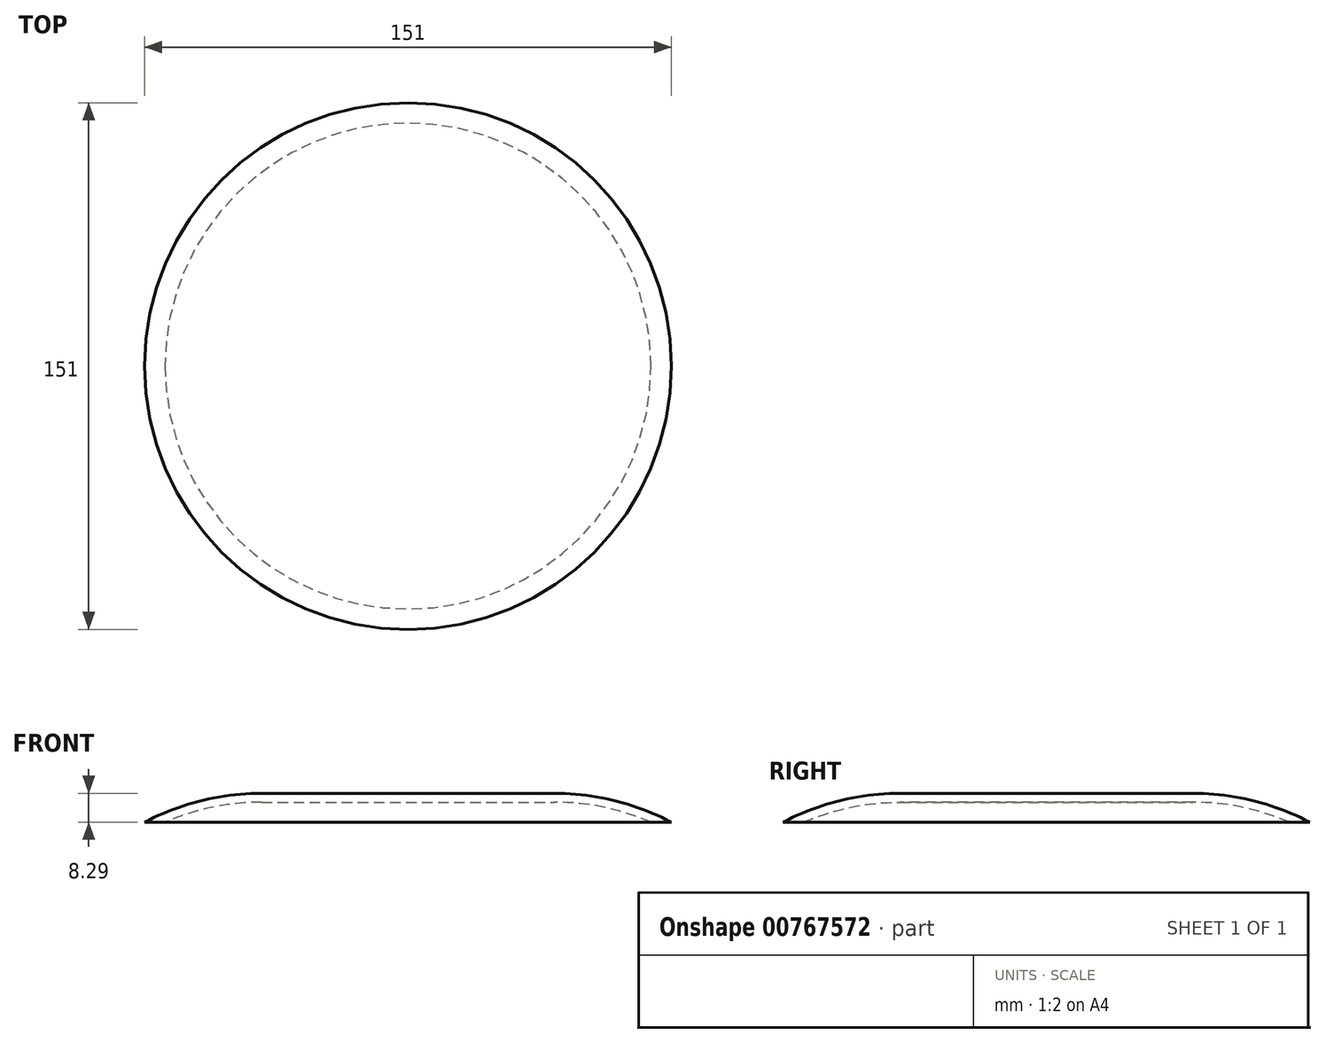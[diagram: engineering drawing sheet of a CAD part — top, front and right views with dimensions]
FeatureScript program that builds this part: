
annotation { "Feature Type Name" : "Feature", "Feature Type Description" : "" }
export const myFeature = defineFeature(function(context is Context, id is Id, definition is map)
    precondition{}
    {
        {
            var Q0;
            Q0=qCreatedBy(makeId("Top.planeOp"),FACE);
            var sketch = newSketch(context, id + "F0", { "sketchPlane" : qUnion([Q0])});
            skCircle(sketch, "E0", {"center": v(0, 0) * mm, "radius": 75.5 * mm});
            skSolve(sketch);
        }
        {
            var Q0;
            Q0=makeQuery(id+"F0.imprint","IMPRINT",FACE,{"disambiguationData":[TD([[makeQuery(id+"F0.imprint","IMPRINT",EDGE,{"derivedFrom":sQuery(id+"F0.wireOp",EDGE,"E0")}),1.0]])]});
            extrude(context, id + "F1", {"entities" : qUnion([Q0]), "depth" : 8.3 * mm, "offsetDistance" : 25.4 * mm});
        }
        {
            var Q0;
            Q0=makeQuery(id+"F1.opExtrude","CAP_FACE",FACE,{"disambiguationData":[OSD([sQuery(id+"F0.wireOp",EDGE,"E0")])],"isStart":false});
            var sketch = newSketch(context, id + "F2", { "sketchPlane" : qUnion([Q0])});
            skCircle(sketch, "E1", {"center": v(0, 0) * mm, "radius": 75.5 * mm});
            skCircle(sketch, "E2", {"center": v(0, 0) * mm, "radius": 58.3 * mm});
            skSolve(sketch);
        }
        {
            var Q0;
            Q0=makeQuery(id+"F1.opExtrude","CAP_EDGE",EDGE,{"disambiguationData":[OSD([sQuery(id+"F0.wireOp",EDGE,"E0")])],"isStart":false});
            fillet(context, id + "F3", {"entities" : qUnion([Q0]), "radius" : 72.01 * mm, "tangentPropagation" : true, "allowEdgeOverflow" : false});
        }
        {
            var Q0;
            Q0=makeQuery(id+"F1.opExtrude","CAP_FACE",FACE,{"disambiguationData":[OSD([sQuery(id+"F0.wireOp",EDGE,"E0")])],"isStart":true});
            shell(context, id + "F4", {"entities" : qUnion([Q0]), "thickness" : 2.54 * mm});
        }
    });
